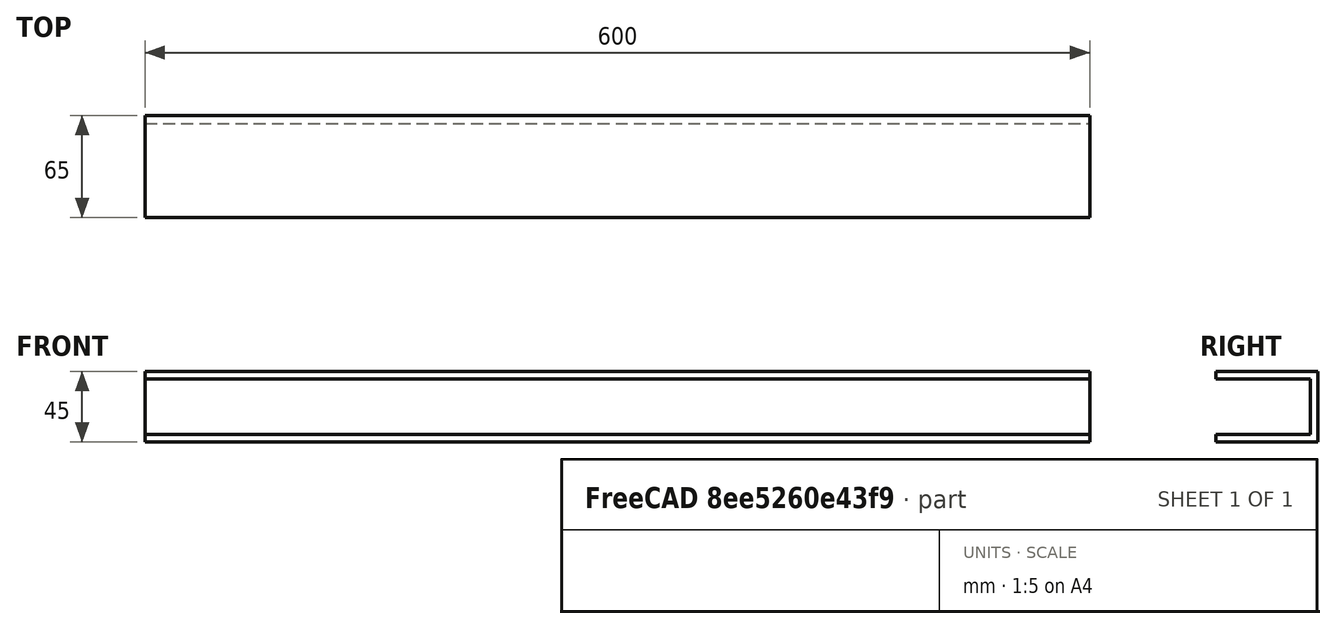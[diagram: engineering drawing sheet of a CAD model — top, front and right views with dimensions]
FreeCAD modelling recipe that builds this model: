
FCSTD DOCUMENT  (FreeCAD 0.21R33771 (Git))
Label: wellhofer-frame-center
License: All rights reserved
LicenseURL: https://en.wikipedia.org/wiki/All_rights_reserved
objects: Sketcher::SketchObject×1, PartDesign::Pad×1, PartDesign::Body×1
note: 4 computed .brp shape members not serialized (recipe doc carries the construction recipe); baked Part::Feature solids carry a one-line shape summary decoded from their .brp

FEATURE [Sketcher::SketchObject] Sketch
  FullyConstrained = true
  MapMode = 5
  Placement = pos=(0,0,0) rot=(0.57735,0.57735,0.57735;2.0944rad)
  Support = -> [YZ_Plane]
  sketch-geometry (8):
    g0: LineSegment StartX=0 StartY=0 StartZ=0 EndX=65 EndY=0 EndZ=0
    g1: LineSegment StartX=65 StartY=0 StartZ=0 EndX=65 EndY=45 EndZ=0
    g2: LineSegment StartX=65 StartY=45 StartZ=0 EndX=0 EndY=45 EndZ=0
    g3: LineSegment StartX=0 StartY=45 StartZ=0 EndX=0 EndY=40 EndZ=0
    g4: LineSegment StartX=0 StartY=40 StartZ=0 EndX=60 EndY=40 EndZ=0
    g5: LineSegment StartX=60 StartY=40 StartZ=0 EndX=60 EndY=5 EndZ=0
    g6: LineSegment StartX=60 StartY=5 StartZ=0 EndX=0 EndY=5 EndZ=0
    g7: LineSegment StartX=0 StartY=5 StartZ=0 EndX=0 EndY=0 EndZ=0
  constraints (23):
    c: Coincident(g0,g-1)
    c: PointOnObject(g0,g-1)
    c: Coincident(g1,g0)
    c: Vertical(g1)
    c: Coincident(g2,g1)
    c: PointOnObject(g2,g-2)
    c: Horizontal(g2)
    c: Coincident(g3,g2)
    c: PointOnObject(g3,g-2)
    c: Coincident(g4,g3)
    c: Horizontal(g4)
    c: Coincident(g5,g4)
    c: Vertical(g5)
    c: Coincident(g6,g5)
    c: Coincident(g7,g6)
    c: Coincident(g7,g0)
    c: Vertical(g7)
    c: DistanceX(g0,g0) = 65
    c: DistanceX(g4,g4) = 60
    c: DistanceY(g1,g1) = 45
    c: DistanceY(g3,g3) = 5
    c: DistanceY(g7,g7) = 5
    c: DistanceY(g5,g5) = 35
FEATURE [PartDesign::Pad] Pad
  Direction = (1,-2e-16,3e-16)
  Length = 600
  Length2 = 10
  Placement = pos=(0,0,0) rot=(1,1,1;2.0944rad)
  Profile = -> Sketch
  ReferenceAxis = -> Sketch [N_Axis]
  Type = 0
FEATURE [PartDesign::Body] Body
  Group = -> [Sketch,Pad]
  Origin = -> Origin
  Tip = -> Pad
